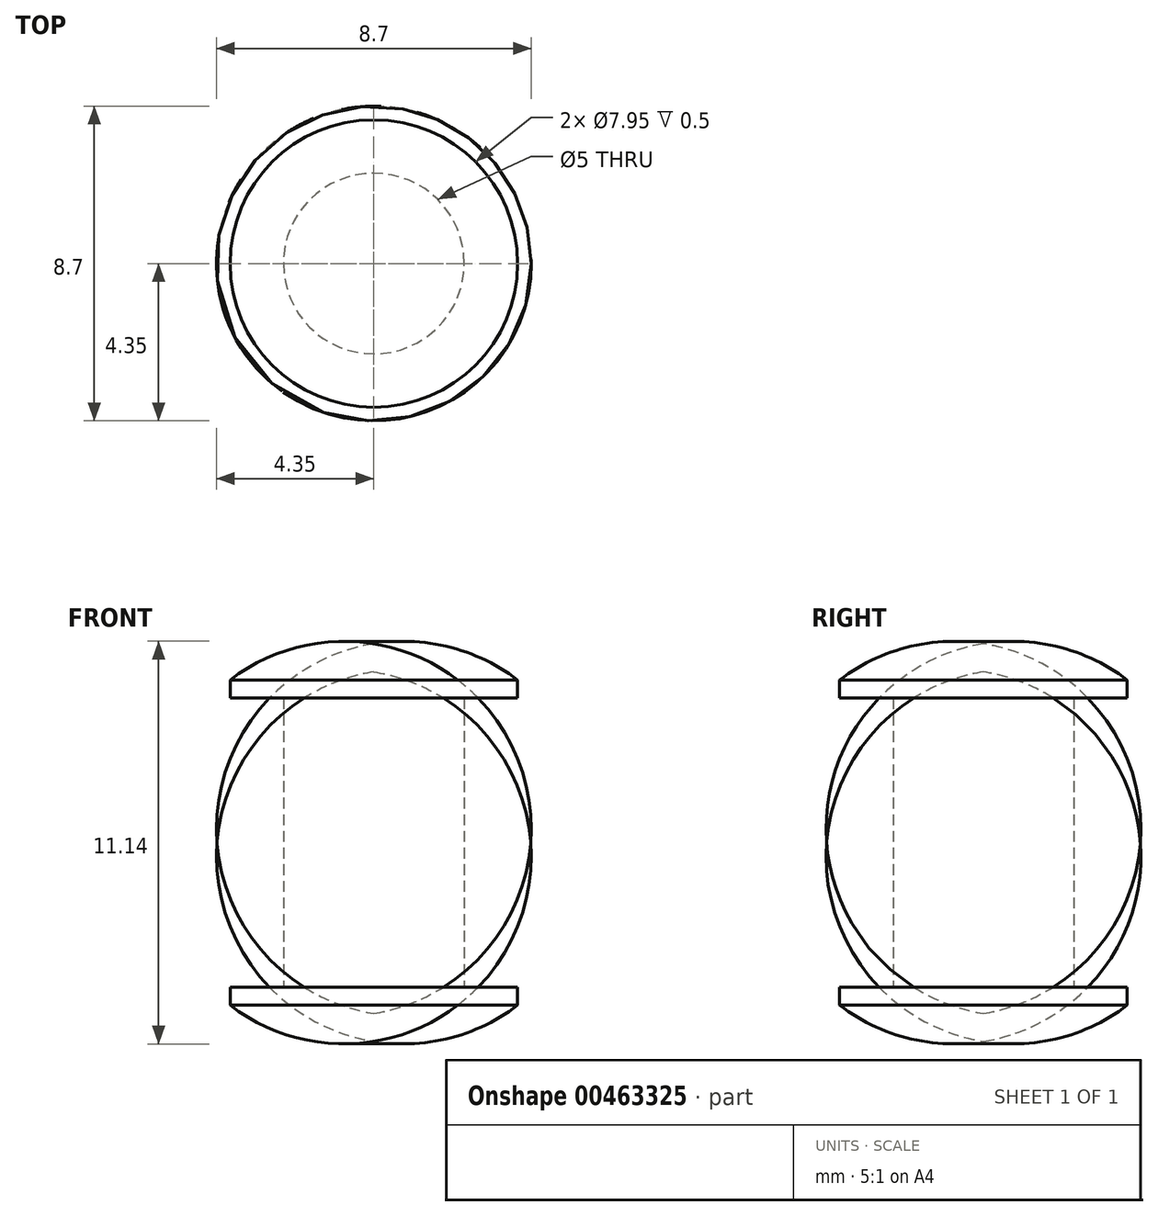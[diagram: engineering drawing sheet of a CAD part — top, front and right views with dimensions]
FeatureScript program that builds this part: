
annotation { "Feature Type Name" : "Feature", "Feature Type Description" : "" }
export const myFeature = defineFeature(function(context is Context, id is Id, definition is map)
    precondition{}
    {
        {
            var Q0;
            Q0=qCreatedBy(makeId("Front.planeOp"),FACE);
            var sketch = newSketch(context, id + "F0", { "sketchPlane" : qUnion([Q0])});
            skLineSegment(sketch, "E0", {"start": v(0, 0) * mm, "end": v(-2.5, 0) * mm});
            skLineSegment(sketch, "E1", {"start": v(-2.5, 0) * mm, "end": v(-2.5, 4) * mm});
            skLineSegment(sketch, "E2", {"start": v(-2.5, 4) * mm, "end": v(-3.97, 4) * mm});
            skLineSegment(sketch, "E3", {"start": v(-3.97, 4) * mm, "end": v(-3.97, 4.5) * mm});
            skArc(sketch, "E4", {"start": v(0, 5.5) * mm, "mid": v(-2.1, 5.4) * mm, "end": v(-3.97, 4.5) * mm});
            skLineSegment(sketch, "E5", {"start": v(0, 0) * mm, "end": v(0, 5.5) * mm});
            skSolve(sketch);
        }
        {
            var Q0;
            Q0=makeQuery(id+"F0.imprint","IMPRINT",FACE,{"disambiguationData":[TD([[makeQuery(id+"F0.imprint","IMPRINT",EDGE,{"derivedFrom":sQuery(id+"F0.wireOp",EDGE,"E0")}),-1.0]])]});
            var Q1;
            Q1=sQuery(id+"F0.wireOp",EDGE,"E5");
            revolve(context, id + "F1", {"entities" : qUnion([Q0]), "axis" : qUnion([Q1]), "revolveType" : RevolveType.FULL});
        }
        {
            var Q0;
            Q0=makeQuery(id+"F1.opRevolve","SWEPT_BODY",BODY,{"disambiguationData":[OSD([sQuery(id+"F0.wireOp",EDGE,"E0"),sQuery(id+"F0.wireOp",EDGE,"E1"),sQuery(id+"F0.wireOp",EDGE,"E2"),sQuery(id+"F0.wireOp",EDGE,"E3"),sQuery(id+"F0.wireOp",EDGE,"E4"),sQuery(id+"F0.wireOp",EDGE,"E5")])]});
            var Q1;
            Q1=makeQuery(id+"F1.opRevolve","SWEPT_FACE",FACE,{"disambiguationData":[OSD([sQuery(id+"F0.wireOp",EDGE,"E0")])]});
            mirror(context, id + "F2", {"operationType" : NewBodyOperationType.ADD, "entities" : qUnion([Q0]), "mirrorPlane" : qUnion([Q1])});
        }
    });
